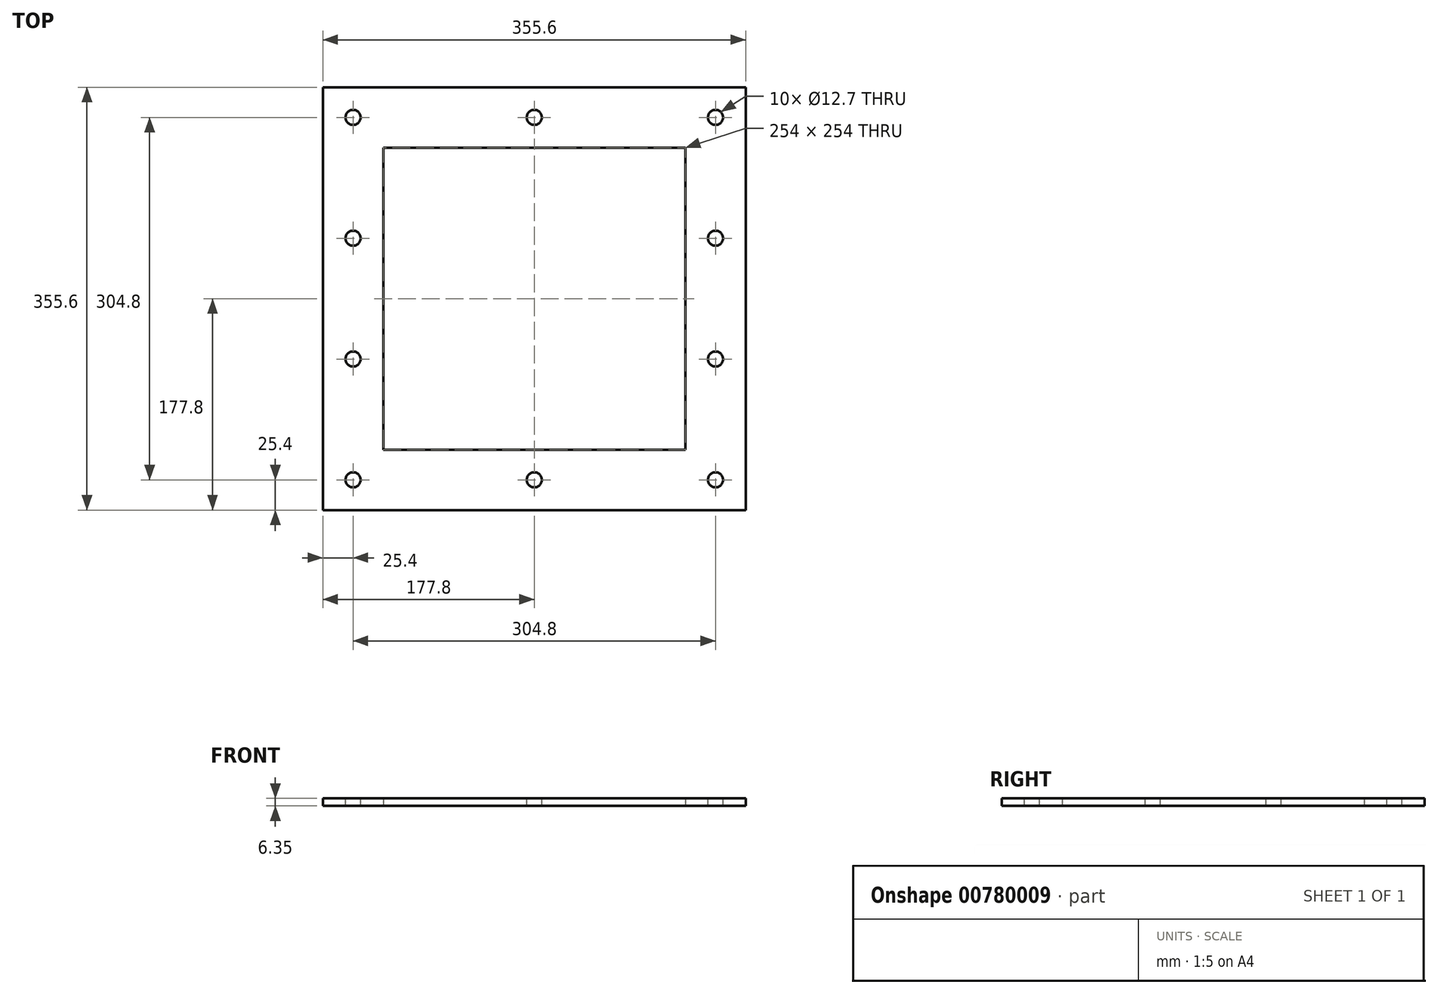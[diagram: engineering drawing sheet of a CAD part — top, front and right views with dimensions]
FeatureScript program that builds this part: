
annotation { "Feature Type Name" : "Feature", "Feature Type Description" : "" }
export const myFeature = defineFeature(function(context is Context, id is Id, definition is map)
    precondition{}
    {
        {
            var Q0;
            Q0=qCreatedBy(makeId("Top.planeOp"),FACE);
            var sketch = newSketch(context, id + "F0", { "sketchPlane" : qUnion([Q0])});
            skLineSegment(sketch, "E0.bottom", {"start": v(-177.8, -177.8) * mm, "end": v(177.8, -177.8) * mm});
            skLineSegment(sketch, "E0.top", {"start": v(-177.8, 177.8) * mm, "end": v(177.8, 177.8) * mm});
            skLineSegment(sketch, "E0.left", {"start": v(-177.8, -177.8) * mm, "end": v(-177.8, 177.8) * mm});
            skLineSegment(sketch, "E0.right", {"start": v(177.8, -177.8) * mm, "end": v(177.8, 177.8) * mm});
            skPoint(sketch, "E0.middle", {"position": v(0, 0) * mm});
            skLineSegment(sketch, "E1.bottom", {"start": v(-127, -127) * mm, "end": v(127, -127) * mm});
            skLineSegment(sketch, "E1.top", {"start": v(-127, 127) * mm, "end": v(127, 127) * mm});
            skLineSegment(sketch, "E1.left", {"start": v(-127, -127) * mm, "end": v(-127, 127) * mm});
            skLineSegment(sketch, "E1.right", {"start": v(127, -127) * mm, "end": v(127, 127) * mm});
            skSolve(sketch);
        }
        {
            var Q0;
            Q0 = qSketchRegion(id + "F0", true);
            extrude(context, id + "F1", {"entities" : qUnion([Q0]), "depth" : 6.35 * mm, "offsetDistance" : 25.4 * mm});
        }
        {
            var Q0;
            Q0=makeQuery(id+"F1.opExtrude","CAP_FACE",FACE,{"disambiguationData":[OSD([sQuery(id+"F0.wireOp",EDGE,"E0.bottom"),sQuery(id+"F0.wireOp",EDGE,"E0.top"),sQuery(id+"F0.wireOp",EDGE,"E0.left"),sQuery(id+"F0.wireOp",EDGE,"E0.right"),sQuery(id+"F0.wireOp",EDGE,"E1.bottom"),sQuery(id+"F0.wireOp",EDGE,"E1.top"),sQuery(id+"F0.wireOp",EDGE,"E1.left"),sQuery(id+"F0.wireOp",EDGE,"E1.right")])],"isStart":false});
            var sketch = newSketch(context, id + "F2", { "sketchPlane" : qUnion([Q0])});
            skLineSegment(sketch, "E2", {"start": v(-177.8, 0) * mm, "end": v(177.8, 0) * mm, "construction": true});
            skCircle(sketch, "E3", {"center": v(-152.4, -50.8) * mm, "radius": 6.35 * mm});
            skCircle(sketch, "E4", {"center": v(-152.4, -152.4) * mm, "radius": 6.35 * mm});
            skCircle(sketch, "E5", {"center": v(0, -152.4) * mm, "radius": 6.35 * mm});
            skCircle(sketch, "E6", {"center": v(152.4, -152.4) * mm, "radius": 6.35 * mm});
            skCircle(sketch, "E7", {"center": v(152.4, -50.8) * mm, "radius": 6.35 * mm});
            skCircle(sketch, "E8.MirrorC", {"center": v(152.4, 50.8) * mm, "radius": 6.35 * mm});
            skCircle(sketch, "E9.MirrorC", {"center": v(152.4, 152.4) * mm, "radius": 6.35 * mm});
            skCircle(sketch, "E10.MirrorC", {"center": v(0, 152.4) * mm, "radius": 6.35 * mm});
            skCircle(sketch, "E11.MirrorC", {"center": v(-152.4, 152.4) * mm, "radius": 6.35 * mm});
            skCircle(sketch, "E12.MirrorC", {"center": v(-152.4, 50.8) * mm, "radius": 6.35 * mm});
            skSolve(sketch);
        }
        {
            var Q0;
            Q0 = qSketchRegion(id + "F2", true);
            extrude(context, id + "F3", {"entities" : qUnion([Q0]), "operationType" : NewBodyOperationType.REMOVE, "oppositeDirection" : true, "depth" : 25.4 * mm, "offsetDistance" : 25.4 * mm});
        }
    });
